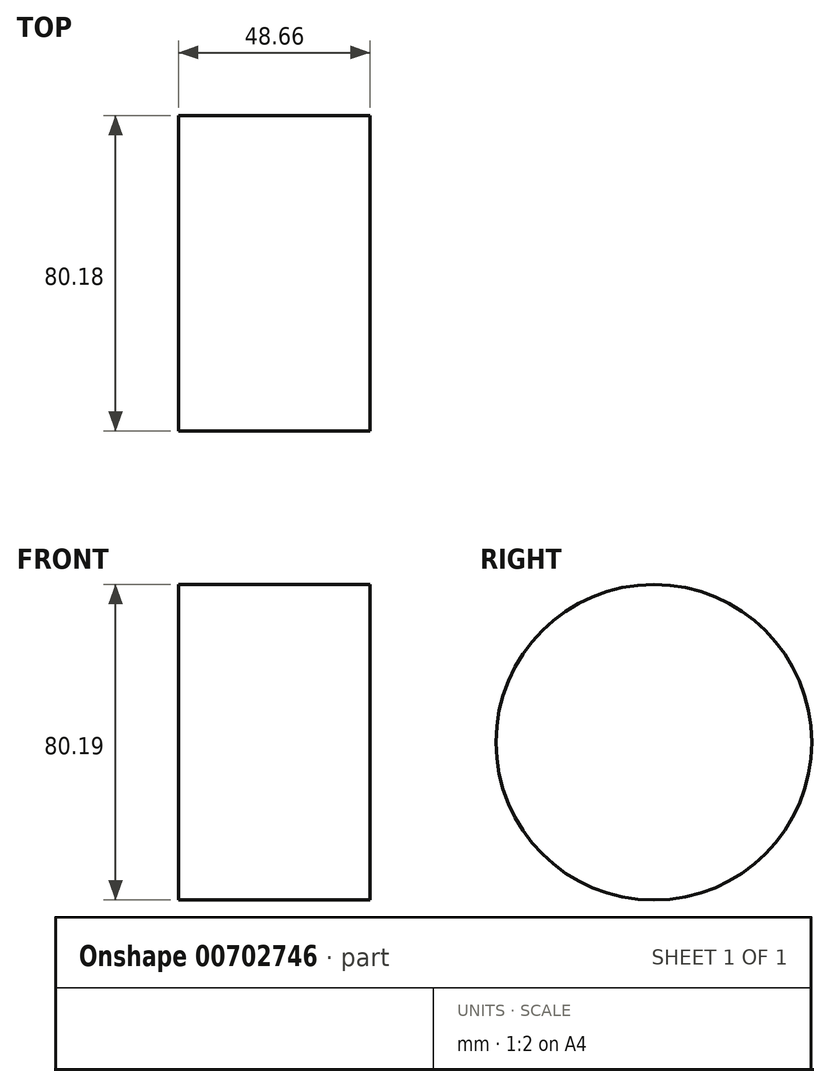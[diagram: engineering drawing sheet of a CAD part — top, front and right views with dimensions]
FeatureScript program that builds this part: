
annotation { "Feature Type Name" : "Feature", "Feature Type Description" : "" }
export const myFeature = defineFeature(function(context is Context, id is Id, definition is map)
    precondition{}
    {
        {
            var Q0;
            Q0=qCreatedBy(makeId("Right.planeOp"),FACE);
            var sketch = newSketch(context, id + "F0", { "sketchPlane" : qUnion([Q0])});
            skCircle(sketch, "E0", {"center": v(-11.77, 23.77) * mm, "radius": 40.1 * mm});
            skSolve(sketch);
        }
        {
            var Q0;
            Q0=makeQuery(id+"F0.imprint","IMPRINT",FACE,{"disambiguationData":[TD([[makeQuery(id+"F0.imprint","IMPRINT",EDGE,{"derivedFrom":sQuery(id+"F0.wireOp",EDGE,"E0")}),1.0]])]});
            extrude(context, id + "F1", {"entities" : qUnion([Q0]), "depth" : 48.66 * mm, "offsetDistance" : 25.4 * mm});
        }
    });
